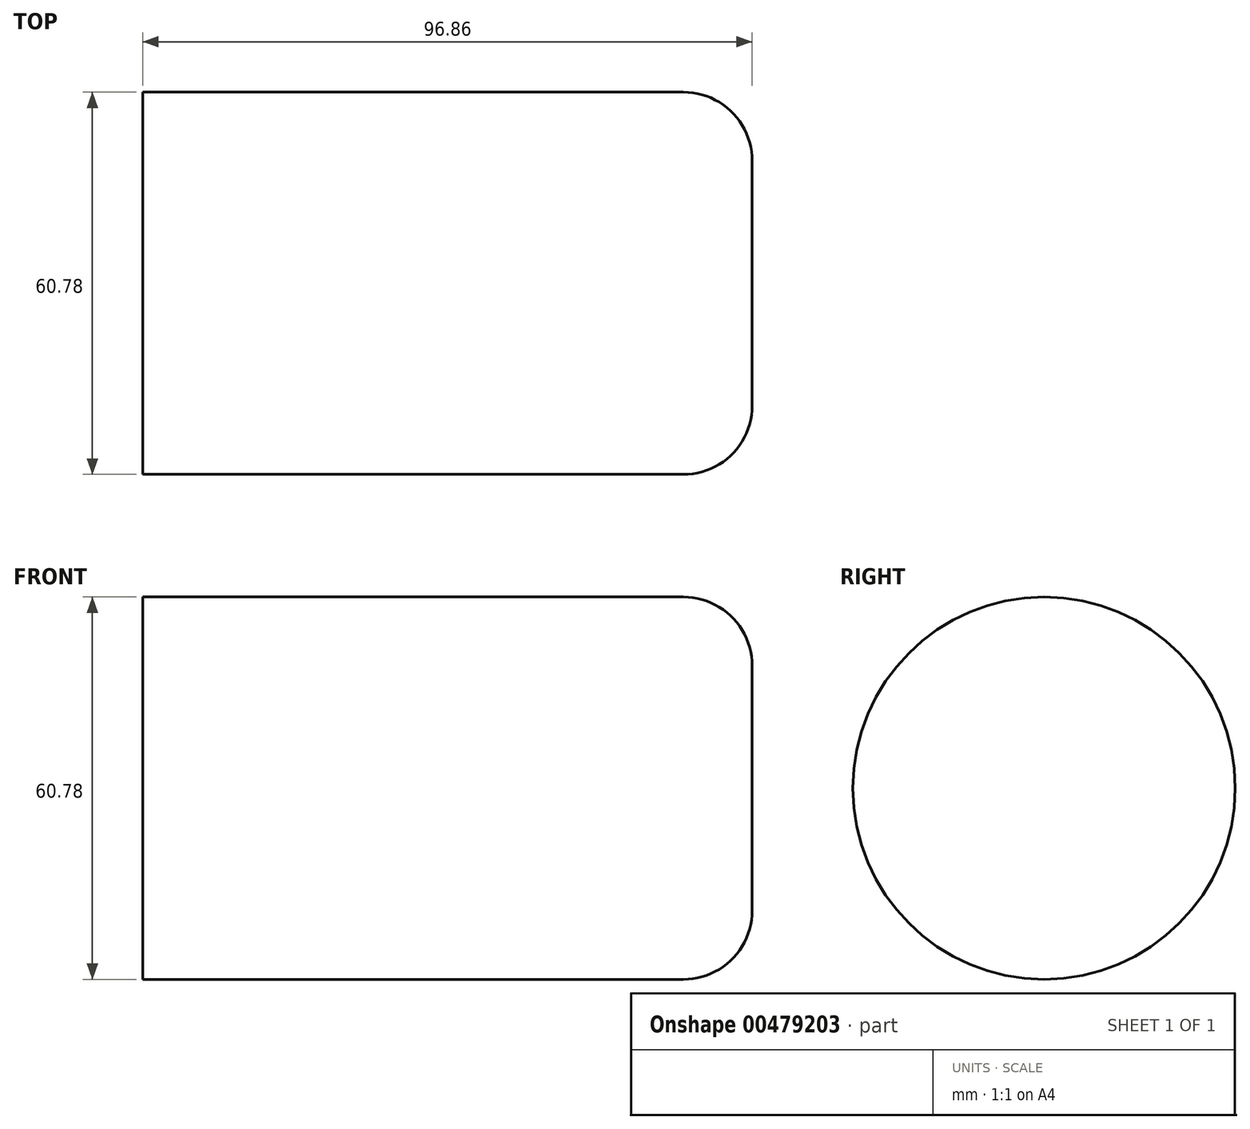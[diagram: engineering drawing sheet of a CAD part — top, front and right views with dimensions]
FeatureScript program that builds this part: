
annotation { "Feature Type Name" : "Feature", "Feature Type Description" : "" }
export const myFeature = defineFeature(function(context is Context, id is Id, definition is map)
    precondition{}
    {
        {
            var Q0;
            Q0=qCreatedBy(makeId("Right.planeOp"),FACE);
            var sketch = newSketch(context, id + "F0", { "sketchPlane" : qUnion([Q0])});
            skCircle(sketch, "E0", {"center": v(0, 0) * mm, "radius": 30.39 * mm});
            skSolve(sketch);
        }
        {
            var Q0;
            Q0 = qSketchRegion(id + "F0", true);
            extrude(context, id + "F1", {"entities" : qUnion([Q0]), "depth" : 96.86 * mm});
        }
        {
            var Q0;
            Q0=makeQuery(id+"F1.opExtrude","CAP_FACE",FACE,{"disambiguationData":[OSD([sQuery(id+"F0.wireOp",EDGE,"E0")])],"isStart":false});
            fillet(context, id + "F2", {"entities" : qUnion([Q0]), "radius" : 10.93 * mm, "tangentPropagation" : true, "allowEdgeOverflow" : false});
        }
    });
